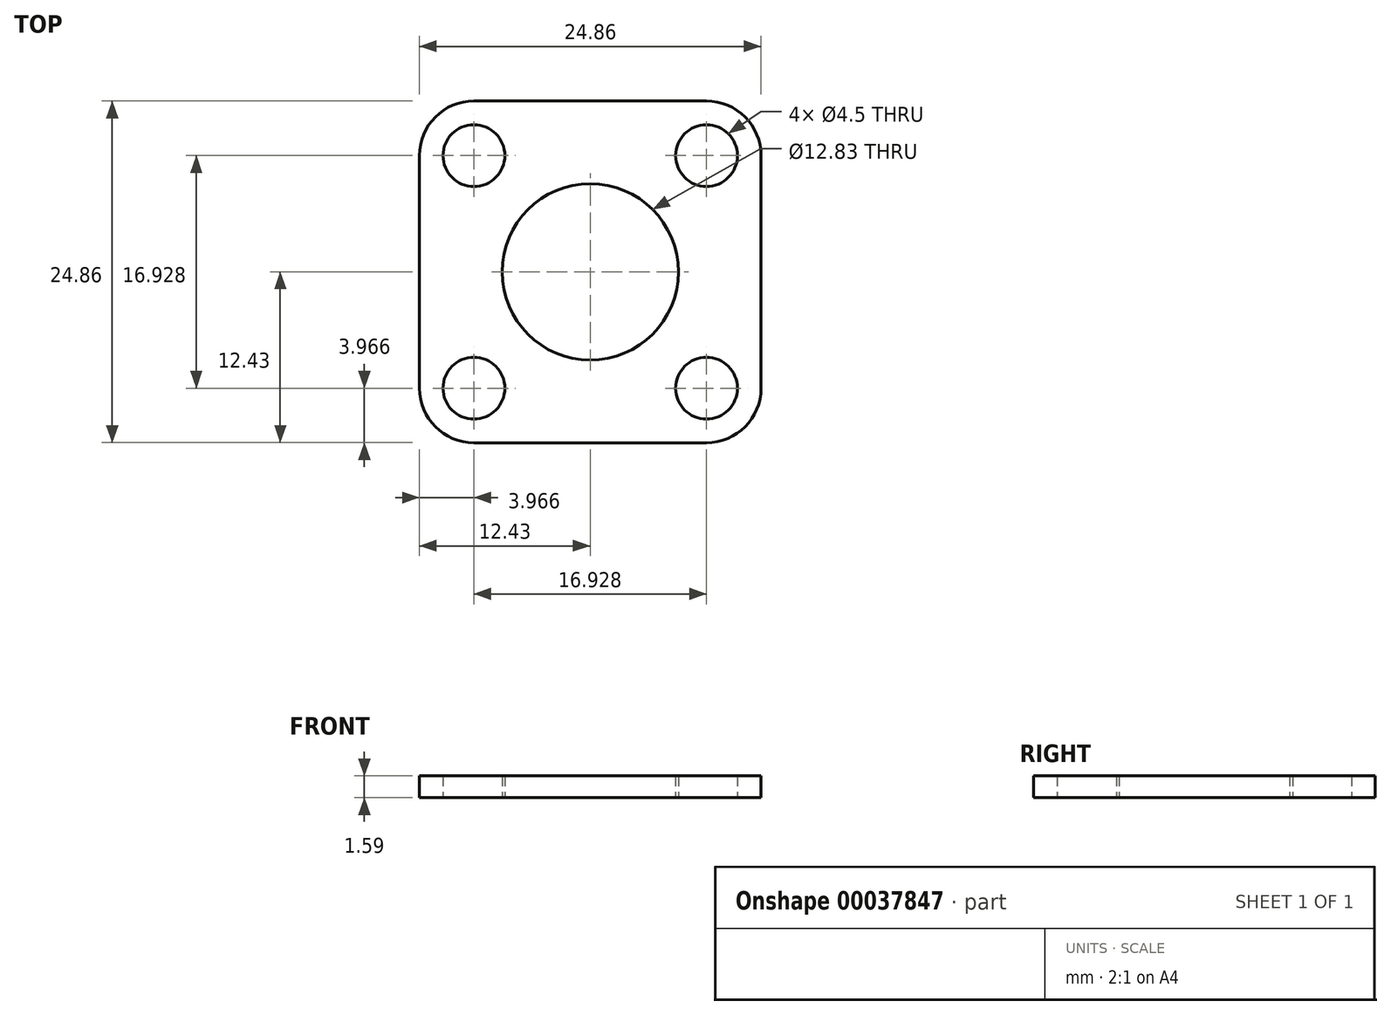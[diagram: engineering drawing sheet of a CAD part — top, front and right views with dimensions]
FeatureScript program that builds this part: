
annotation { "Feature Type Name" : "Feature", "Feature Type Description" : "" }
export const myFeature = defineFeature(function(context is Context, id is Id, definition is map)
    precondition{}
    {
        {
            var Q0;
            Q0=qCreatedBy(makeId("Top.planeOp"),FACE);
            var sketch = newSketch(context, id + "F0", { "sketchPlane" : qUnion([Q0])});
            skLineSegment(sketch, "E0.rect.bottom", {"start": v(-12.43, 12.43) * mm, "end": v(12.43, 12.43) * mm});
            skLineSegment(sketch, "E0.rect.top", {"start": v(-12.43, -12.43) * mm, "end": v(12.43, -12.43) * mm});
            skLineSegment(sketch, "E0.rect.left", {"start": v(-12.43, 12.43) * mm, "end": v(-12.43, -12.43) * mm});
            skLineSegment(sketch, "E0.rect.right", {"start": v(12.43, 12.43) * mm, "end": v(12.43, -12.43) * mm});
            skPoint(sketch, "E0.rect.middle", {"position": v(0, 0) * mm});
            skLineSegment(sketch, "E1.rect.bottom", {"start": v(-8.46, 8.46) * mm, "end": v(8.46, 8.46) * mm, "construction": true});
            skLineSegment(sketch, "E1.rect.top", {"start": v(-8.46, -8.46) * mm, "end": v(8.46, -8.46) * mm, "construction": true});
            skLineSegment(sketch, "E1.rect.left", {"start": v(-8.46, 8.46) * mm, "end": v(-8.46, -8.46) * mm, "construction": true});
            skLineSegment(sketch, "E1.rect.right", {"start": v(8.46, 8.46) * mm, "end": v(8.46, -8.46) * mm, "construction": true});
            skCircle(sketch, "E2", {"center": v(-8.46, 8.46) * mm, "radius": 3.97 * mm, "construction": true});
            skCircle(sketch, "E3", {"center": v(0, 0) * mm, "radius": 8 * mm, "construction": true});
            skCircle(sketch, "E4", {"center": v(0, 0) * mm, "radius": 6.41 * mm});
            skCircle(sketch, "E5", {"center": v(-8.46, 8.46) * mm, "radius": 2.25 * mm});
            skCircle(sketch, "E6", {"center": v(8.46, 8.46) * mm, "radius": 2.25 * mm});
            skCircle(sketch, "E7", {"center": v(8.46, -8.46) * mm, "radius": 2.25 * mm});
            skCircle(sketch, "E8", {"center": v(-8.46, -8.46) * mm, "radius": 2.25 * mm});
            skSolve(sketch);
        }
        {
            var Q0;
            Q0 = qSketchRegion(id + "F0", true);
            extrude(context, id + "F1", {"entities" : qUnion([Q0]), "depth" : 1.59 * mm});
        }
        {
            var Q0;
            Q0=makeQuery(id+"F1.opExtrude","SWEPT_EDGE",EDGE,{"disambiguationData":[OSD([sQuery(id+"F0.wireOp",EDGE,"E0.rect.bottom"),sQuery(id+"F0.wireOp",EDGE,"E0.rect.left")])]});
            var Q1;
            Q1=makeQuery(id+"F1.opExtrude","SWEPT_EDGE",EDGE,{"disambiguationData":[OSD([sQuery(id+"F0.wireOp",EDGE,"E0.rect.top"),sQuery(id+"F0.wireOp",EDGE,"E0.rect.left")])]});
            var Q2;
            Q2=makeQuery(id+"F1.opExtrude","SWEPT_EDGE",EDGE,{"disambiguationData":[OSD([sQuery(id+"F0.wireOp",EDGE,"E0.rect.top"),sQuery(id+"F0.wireOp",EDGE,"E0.rect.right")])]});
            var Q3;
            Q3=makeQuery(id+"F1.opExtrude","SWEPT_EDGE",EDGE,{"disambiguationData":[OSD([sQuery(id+"F0.wireOp",EDGE,"E0.rect.bottom"),sQuery(id+"F0.wireOp",EDGE,"E0.rect.right")])]});
            fillet(context, id + "F2", {"entities" : qUnion([Q0, Q1, Q2, Q3]), "radius" : 3.97 * mm, "tangentPropagation" : true, "allowEdgeOverflow" : false});
        }
    });
